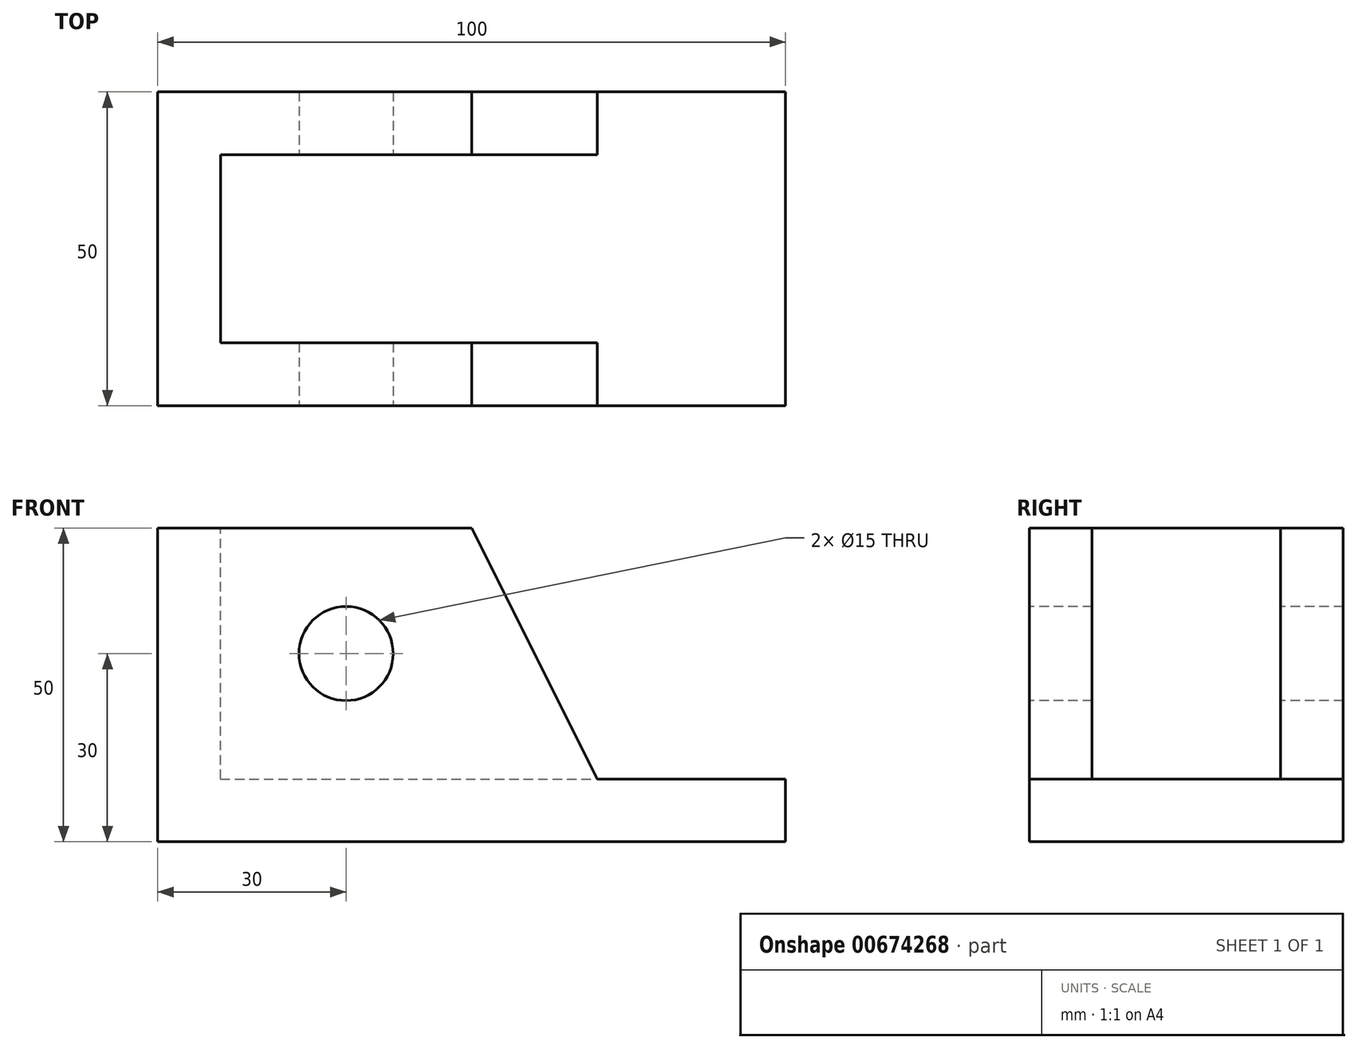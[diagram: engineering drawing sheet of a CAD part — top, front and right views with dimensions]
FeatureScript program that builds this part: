
annotation { "Feature Type Name" : "Feature", "Feature Type Description" : "" }
export const myFeature = defineFeature(function(context is Context, id is Id, definition is map)
    precondition{}
    {
        {
            var Q0;
            Q0=qCreatedBy(makeId("Front.planeOp"),FACE);
            var sketch = newSketch(context, id + "F0", { "sketchPlane" : qUnion([Q0])});
            skLineSegment(sketch, "E0", {"start": v(0, 0) * mm, "end": v(100, 0) * mm});
            skLineSegment(sketch, "E1", {"start": v(100, 0) * mm, "end": v(100, 10) * mm});
            skLineSegment(sketch, "E2", {"start": v(100, 10) * mm, "end": v(70, 10) * mm});
            skLineSegment(sketch, "E3", {"start": v(70, 10) * mm, "end": v(50, 50) * mm});
            skLineSegment(sketch, "E4", {"start": v(50, 50) * mm, "end": v(0, 50) * mm});
            skLineSegment(sketch, "E5", {"start": v(0, 50) * mm, "end": v(0, 0) * mm});
            skSolve(sketch);
        }
        {
            var Q0;
            Q0 = qSketchRegion(id + "F0", true);
            extrude(context, id + "F1", {"entities" : qUnion([Q0]), "endBound" : BoundingType.SYMMETRIC, "depth" : 50 * mm, "offsetDistance" : 25 * mm});
        }
        {
            var Q0;
            Q0=makeQuery(id+"F1.opExtrude","SWEPT_FACE",FACE,{"disambiguationData":[OSD([sQuery(id+"F0.wireOp",EDGE,"E4")])]});
            var sketch = newSketch(context, id + "F2", { "sketchPlane" : qUnion([Q0])});
            skLineSegment(sketch, "E6", {"start": v(10, 15) * mm, "end": v(70, 15) * mm});
            skLineSegment(sketch, "E7", {"start": v(70, 15) * mm, "end": v(70, -15) * mm});
            skLineSegment(sketch, "E8", {"start": v(70, -15) * mm, "end": v(10, -15) * mm});
            skLineSegment(sketch, "E9", {"start": v(10, -15) * mm, "end": v(10, 15) * mm});
            skSolve(sketch);
        }
        {
            var Q0;
            {var subQ0=sQuery(id+"F2.wireOp",EDGE,"E7");Q0=makeQuery(id+"F2.imprint","IMPRINT",FACE,{"disambiguationData":[TD([[makeQuery(id+"F2.imprint","IMPRINT",EDGE,{"derivedFrom":subQ0}),-1.0]])]});}
            var Q1;
            {var subQ0=sQuery(id+"F2.wireOp",EDGE,"E9");Q1=makeQuery(id+"F2.imprint","IMPRINT",FACE,{"disambiguationData":[TD([[makeQuery(id+"F2.imprint","IMPRINT",EDGE,{"derivedFrom":subQ0}),-1.0]])]});}
            var Q2;
            Q2=makeQuery(id+"F1.opExtrude","SWEPT_FACE",FACE,{"disambiguationData":[OSD([sQuery(id+"F0.wireOp",EDGE,"E2")])]});
            extrude(context, id + "F3", {"entities" : qUnion([Q0, Q1]), "operationType" : NewBodyOperationType.REMOVE, "endBound" : BoundingType.UP_TO_SURFACE, "oppositeDirection" : true, "depth" : 25 * mm, "endBoundEntityFace" : qUnion([Q2]), "offsetDistance" : 25 * mm});
        }
        {
            var Q0;
            Q0=makeQuery(id+"F1.opExtrude","CAP_FACE",FACE,{"disambiguationData":[OSD([sQuery(id+"F0.wireOp",EDGE,"E0"),sQuery(id+"F0.wireOp",EDGE,"E1"),sQuery(id+"F0.wireOp",EDGE,"E2"),sQuery(id+"F0.wireOp",EDGE,"E3"),sQuery(id+"F0.wireOp",EDGE,"E4"),sQuery(id+"F0.wireOp",EDGE,"E5")])],"isStart":false});
            var sketch = newSketch(context, id + "F4", { "sketchPlane" : qUnion([Q0])});
            skCircle(sketch, "E10", {"center": v(30, 30) * mm, "radius": 7.5 * mm});
            skSolve(sketch);
        }
        {
            var Q0;
            Q0 = qSketchRegion(id + "F4", true);
            extrude(context, id + "F5", {"entities" : qUnion([Q0]), "operationType" : NewBodyOperationType.REMOVE, "endBound" : BoundingType.THROUGH_ALL, "oppositeDirection" : true, "depth" : 25 * mm, "offsetDistance" : 25 * mm});
        }
    });
